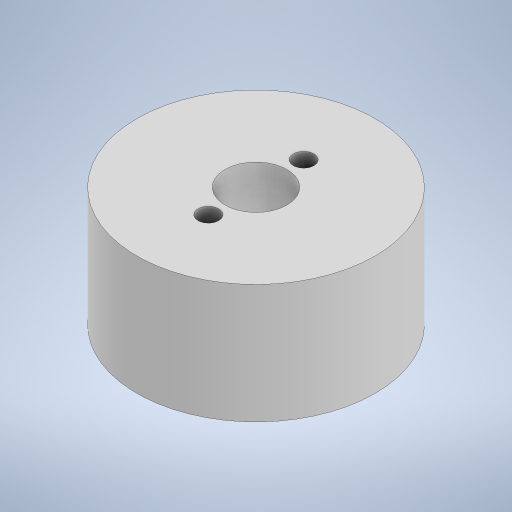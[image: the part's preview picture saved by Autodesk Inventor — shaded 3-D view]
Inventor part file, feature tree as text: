
AUTODESK INVENTOR PART (.ipt)
format: ipt  version: 2024.2 (Build 282272000, 272)  size: 224,256 bytes
history: native  units: in
note: dims shown in document units (in); Inventor stores cm internally (conversion verified against a paired STEP export)
features: extrude x3, sketch x3
ambient origin geometry x8: Origin, YZ Plane, XZ Plane, XY Plane, X Axis, Y Axis, Z Axis, Center Point
bodies: Solid1 (feature_tree)
feature tree (6):
  extrude  "Extrusion1"  Depth=0.26in
  extrude  "Extrusion2"  Depth=0.2in
  extrude  "Extrusion3"  Depth=0.075in
  sketch  "Sketch1"  dims[d0=1.0in d1=0.26in]
  sketch  "Sketch2"  dims[d2=0.5in d3=0.0in d4=0.2in]
  sketch  "Sketch3"  dims[d5=0.2in d6=0.087in d7=0.087in d8=0.175in d9=0.0in d10=0.2in d11=0.4in d12=0.075in d13=0.0in d14=0.087in d15=0.087in]
